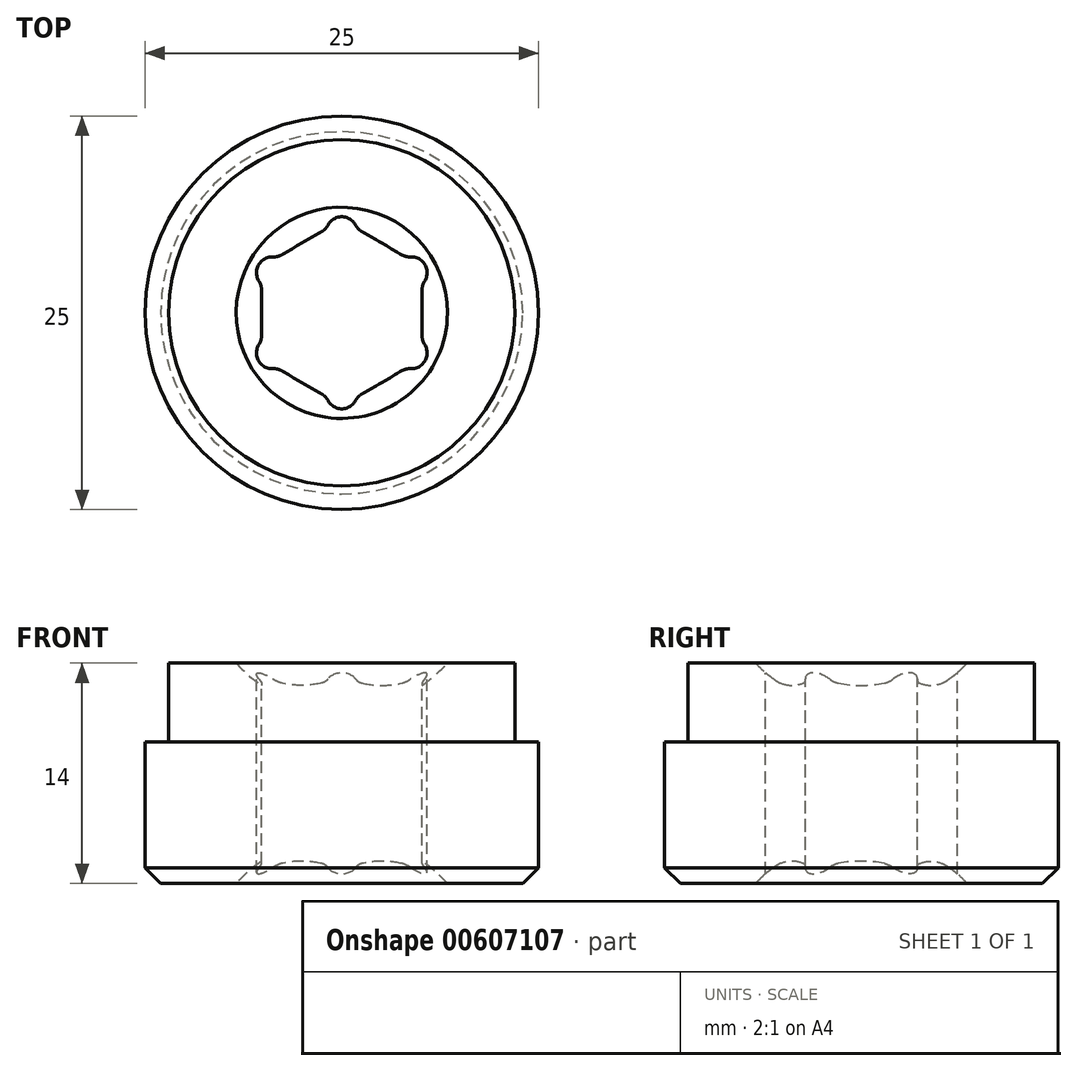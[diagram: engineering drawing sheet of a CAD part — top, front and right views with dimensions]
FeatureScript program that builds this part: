
annotation { "Feature Type Name" : "Feature", "Feature Type Description" : "" }
export const myFeature = defineFeature(function(context is Context, id is Id, definition is map)
    precondition{}
    {
        {
            var Q0;
            Q0=qCreatedBy(makeId("Top.planeOp"),FACE);
            var sketch = newSketch(context, id + "F0", { "sketchPlane" : qUnion([Q0])});
            skCircle(sketch, "E0", {"center": v(0, 0) * mm, "radius": 12.5 * mm});
            skCircle(sketch, "E1.cCircle", {"center": v(0, 0) * mm, "radius": 5.1 * mm, "construction": true});
            skLineSegment(sketch, "E1.0", {"start": v(5.1, -2.94) * mm, "end": v(0, -5.89) * mm});
            skLineSegment(sketch, "E1.1", {"start": v(0, -5.89) * mm, "end": v(-5.1, -2.94) * mm});
            skLineSegment(sketch, "E1.2", {"start": v(-5.1, -2.94) * mm, "end": v(-5.1, 2.94) * mm});
            skLineSegment(sketch, "E1.3", {"start": v(-5.1, 2.94) * mm, "end": v(0, 5.89) * mm});
            skLineSegment(sketch, "E1.4", {"start": v(0, 5.89) * mm, "end": v(5.1, 2.94) * mm});
            skLineSegment(sketch, "E1.5", {"start": v(5.1, 2.94) * mm, "end": v(5.1, -2.94) * mm});
            skPoint(sketch, "E1.0.midPoint", {"position": v(2.55, -4.42) * mm});
            skSolve(sketch);
        }
        {
            var Q0;
            Q0 = qSketchRegion(id + "F0", true);
            extrude(context, id + "F1", {"entities" : qUnion([Q0]), "depth" : 14 * mm, "offsetDistance" : 25 * mm});
        }
        {
            var Q0;
            Q0=makeQuery(id+"F1.opExtrude","CAP_FACE",FACE,{"disambiguationData":[OSD([sQuery(id+"F0.wireOp",EDGE,"E0"),sQuery(id+"F0.wireOp",EDGE,"E1.0"),sQuery(id+"F0.wireOp",EDGE,"E1.1"),sQuery(id+"F0.wireOp",EDGE,"E1.2"),sQuery(id+"F0.wireOp",EDGE,"E1.3"),sQuery(id+"F0.wireOp",EDGE,"E1.4"),sQuery(id+"F0.wireOp",EDGE,"E1.5")])],"isStart":false});
            var sketch = newSketch(context, id + "F2", { "sketchPlane" : qUnion([Q0])});
            skCircle(sketch, "E2", {"center": v(0, 0) * mm, "radius": 11 * mm});
            skCircle(sketch, "E3.0", {"center": v(0, 0) * mm, "radius": 12.5 * mm});
            skSolve(sketch);
        }
        {
            var Q0;
            Q0 = qSketchRegion(id + "F2", true);
            extrude(context, id + "F3", {"entities" : qUnion([Q0]), "operationType" : NewBodyOperationType.REMOVE, "oppositeDirection" : true, "depth" : 5 * mm, "offsetDistance" : 25 * mm});
        }
        {
            var Q0;
            Q0=makeQuery(id+"F1.opExtrude","CAP_FACE",FACE,{"disambiguationData":[OSD([sQuery(id+"F0.wireOp",EDGE,"E0"),sQuery(id+"F0.wireOp",EDGE,"E1.0"),sQuery(id+"F0.wireOp",EDGE,"E1.1"),sQuery(id+"F0.wireOp",EDGE,"E1.2"),sQuery(id+"F0.wireOp",EDGE,"E1.3"),sQuery(id+"F0.wireOp",EDGE,"E1.4"),sQuery(id+"F0.wireOp",EDGE,"E1.5")])],"isStart":false});
            var sketch = newSketch(context, id + "F4", { "sketchPlane" : qUnion([Q0])});
            skCircle(sketch, "E4.cCircle", {"center": v(0, 0) * mm, "radius": 4.42 * mm, "construction": true});
            skLineSegment(sketch, "E4.0", {"start": v(0, 5.1) * mm, "end": v(4.42, 2.55) * mm, "construction": true});
            skLineSegment(sketch, "E4.1", {"start": v(4.42, 2.55) * mm, "end": v(4.42, -2.55) * mm, "construction": true});
            skLineSegment(sketch, "E4.2", {"start": v(4.42, -2.55) * mm, "end": v(0, -5.1) * mm, "construction": true});
            skLineSegment(sketch, "E4.3", {"start": v(0, -5.1) * mm, "end": v(-4.42, -2.55) * mm, "construction": true});
            skLineSegment(sketch, "E4.4", {"start": v(-4.42, -2.55) * mm, "end": v(-4.42, 2.55) * mm, "construction": true});
            skLineSegment(sketch, "E4.5", {"start": v(-4.42, 2.55) * mm, "end": v(0, 5.1) * mm, "construction": true});
            skPoint(sketch, "E4.0.midPoint", {"position": v(2.2, 3.82) * mm});
            skCircle(sketch, "E5", {"center": v(0, 5.1) * mm, "radius": 1 * mm});
            skCircle(sketch, "E6", {"center": v(-4.42, 2.55) * mm, "radius": 1 * mm});
            skCircle(sketch, "E7", {"center": v(-4.42, -2.55) * mm, "radius": 1 * mm});
            skCircle(sketch, "E8", {"center": v(0, -5.1) * mm, "radius": 1 * mm});
            skCircle(sketch, "E9", {"center": v(4.42, -2.55) * mm, "radius": 1 * mm});
            skCircle(sketch, "E10", {"center": v(4.42, 2.55) * mm, "radius": 1 * mm});
            skCircle(sketch, "E11", {"center": v(0, 0) * mm, "radius": 5.1 * mm, "construction": true});
            skSolve(sketch);
        }
        {
            var Q0;
            Q0 = qSketchRegion(id + "F4", true);
            extrude(context, id + "F5", {"entities" : qUnion([Q0]), "operationType" : NewBodyOperationType.REMOVE, "endBound" : BoundingType.THROUGH_ALL, "oppositeDirection" : true, "depth" : 25 * mm, "offsetDistance" : 25 * mm});
        }
        {
            var Q0;
            Q0=makeQuery(id+"F5.boolean.opBoolean","INTERSECT",EDGE,{"derivedFrom":[makeQuery(id+"F1.opExtrude","SWEPT_FACE",FACE,{"disambiguationData":[OSD([sQuery(id+"F0.wireOp",EDGE,"E1.2")])]}),makeQuery(id+"F5.opExtrude","SWEPT_FACE",FACE,{"disambiguationData":[OSD([sQuery(id+"F4.wireOp",EDGE,"E6")])]})]});
            var Q1;
            Q1=makeQuery(id+"F5.boolean.opBoolean","INTERSECT",EDGE,{"derivedFrom":[makeQuery(id+"F1.opExtrude","SWEPT_FACE",FACE,{"disambiguationData":[OSD([sQuery(id+"F0.wireOp",EDGE,"E1.2")])]}),makeQuery(id+"F5.opExtrude","SWEPT_FACE",FACE,{"disambiguationData":[OSD([sQuery(id+"F4.wireOp",EDGE,"E7")])]})]});
            var Q2;
            Q2=makeQuery(id+"F5.boolean.opBoolean","INTERSECT",EDGE,{"derivedFrom":[makeQuery(id+"F1.opExtrude","SWEPT_FACE",FACE,{"disambiguationData":[OSD([sQuery(id+"F0.wireOp",EDGE,"E1.1")])]}),makeQuery(id+"F5.opExtrude","SWEPT_FACE",FACE,{"disambiguationData":[OSD([sQuery(id+"F4.wireOp",EDGE,"E7")])]})]});
            var Q3;
            Q3=makeQuery(id+"F5.boolean.opBoolean","INTERSECT",EDGE,{"derivedFrom":[makeQuery(id+"F1.opExtrude","SWEPT_FACE",FACE,{"disambiguationData":[OSD([sQuery(id+"F0.wireOp",EDGE,"E1.1")])]}),makeQuery(id+"F5.opExtrude","SWEPT_FACE",FACE,{"disambiguationData":[OSD([sQuery(id+"F4.wireOp",EDGE,"E8")])]})]});
            var Q4;
            Q4=makeQuery(id+"F5.boolean.opBoolean","INTERSECT",EDGE,{"derivedFrom":[makeQuery(id+"F1.opExtrude","SWEPT_FACE",FACE,{"disambiguationData":[OSD([sQuery(id+"F0.wireOp",EDGE,"E1.0")])]}),makeQuery(id+"F5.opExtrude","SWEPT_FACE",FACE,{"disambiguationData":[OSD([sQuery(id+"F4.wireOp",EDGE,"E8")])]})]});
            var Q5;
            Q5=makeQuery(id+"F5.boolean.opBoolean","INTERSECT",EDGE,{"derivedFrom":[makeQuery(id+"F1.opExtrude","SWEPT_FACE",FACE,{"disambiguationData":[OSD([sQuery(id+"F0.wireOp",EDGE,"E1.0")])]}),makeQuery(id+"F5.opExtrude","SWEPT_FACE",FACE,{"disambiguationData":[OSD([sQuery(id+"F4.wireOp",EDGE,"E9")])]})]});
            var Q6;
            Q6=makeQuery(id+"F5.boolean.opBoolean","INTERSECT",EDGE,{"derivedFrom":[makeQuery(id+"F1.opExtrude","SWEPT_FACE",FACE,{"disambiguationData":[OSD([sQuery(id+"F0.wireOp",EDGE,"E1.5")])]}),makeQuery(id+"F5.opExtrude","SWEPT_FACE",FACE,{"disambiguationData":[OSD([sQuery(id+"F4.wireOp",EDGE,"E9")])]})]});
            var Q7;
            Q7=makeQuery(id+"F5.boolean.opBoolean","INTERSECT",EDGE,{"derivedFrom":[makeQuery(id+"F1.opExtrude","SWEPT_FACE",FACE,{"disambiguationData":[OSD([sQuery(id+"F0.wireOp",EDGE,"E1.5")])]}),makeQuery(id+"F5.opExtrude","SWEPT_FACE",FACE,{"disambiguationData":[OSD([sQuery(id+"F4.wireOp",EDGE,"E10")])]})]});
            var Q8;
            Q8=makeQuery(id+"F5.boolean.opBoolean","INTERSECT",EDGE,{"derivedFrom":[makeQuery(id+"F1.opExtrude","SWEPT_FACE",FACE,{"disambiguationData":[OSD([sQuery(id+"F0.wireOp",EDGE,"E1.4")])]}),makeQuery(id+"F5.opExtrude","SWEPT_FACE",FACE,{"disambiguationData":[OSD([sQuery(id+"F4.wireOp",EDGE,"E10")])]})]});
            var Q9;
            Q9=makeQuery(id+"F5.boolean.opBoolean","INTERSECT",EDGE,{"derivedFrom":[makeQuery(id+"F1.opExtrude","SWEPT_FACE",FACE,{"disambiguationData":[OSD([sQuery(id+"F0.wireOp",EDGE,"E1.4")])]}),makeQuery(id+"F5.opExtrude","SWEPT_FACE",FACE,{"disambiguationData":[OSD([sQuery(id+"F4.wireOp",EDGE,"E5")])]})]});
            var Q10;
            Q10=makeQuery(id+"F5.boolean.opBoolean","INTERSECT",EDGE,{"derivedFrom":[makeQuery(id+"F1.opExtrude","SWEPT_FACE",FACE,{"disambiguationData":[OSD([sQuery(id+"F0.wireOp",EDGE,"E1.3")])]}),makeQuery(id+"F5.opExtrude","SWEPT_FACE",FACE,{"disambiguationData":[OSD([sQuery(id+"F4.wireOp",EDGE,"E5")])]})]});
            var Q11;
            Q11=makeQuery(id+"F5.boolean.opBoolean","INTERSECT",EDGE,{"derivedFrom":[makeQuery(id+"F1.opExtrude","SWEPT_FACE",FACE,{"disambiguationData":[OSD([sQuery(id+"F0.wireOp",EDGE,"E1.3")])]}),makeQuery(id+"F5.opExtrude","SWEPT_FACE",FACE,{"disambiguationData":[OSD([sQuery(id+"F4.wireOp",EDGE,"E6")])]})]});
            fillet(context, id + "F6", {"entities" : qUnion([Q0, Q1, Q2, Q3, Q4, Q5, Q6, Q7, Q8, Q9, Q10, Q11]), "radius" : 1 * mm, "tangentPropagation" : true, "allowEdgeOverflow" : false});
        }
        {
            var Q0;
            Q0=makeQuery(id+"F3.boolean.opBoolean","COPY",EDGE,{"derivedFrom":makeQuery(id+"F3.opExtrude","CAP_EDGE",EDGE,{"disambiguationData":[OSD([sQuery(id+"F2.wireOp",EDGE,"E2")])],"isStart":true})});
            var Q1;
            Q1=makeQuery(id+"F1.opExtrude","CAP_EDGE",EDGE,{"disambiguationData":[OSD([sQuery(id+"F0.wireOp",EDGE,"E0")])],"isStart":true});
            chamfer(context, id + "F7", {"entities" : qUnion([Q0, Q1]), "width" : 1 * mm, "tangentPropagation" : true});
        }
        {
            var Q0;
            Q0=qCreatedBy(makeId("Right.planeOp"),FACE);
            var sketch = newSketch(context, id + "F8", { "sketchPlane" : qUnion([Q0])});
            skArc(sketch, "E12", {"start": v(0, -15) * mm, "mid": v(9, -6) * mm, "end": v(0, 3) * mm});
            skArc(sketch, "E13", {"start": v(0, 11) * mm, "mid": v(9, 20) * mm, "end": v(0, 29) * mm});
            skLineSegment(sketch, "E14", {"start": v(0, -15) * mm, "end": v(0, 3) * mm});
            skLineSegment(sketch, "E15.trimOffspring", {"start": v(0, 11) * mm, "end": v(0, 29) * mm});
            skSolve(sketch);
        }
        {
            var Q0;
            Q0 = qSketchRegion(id + "F8", true);
            var Q1;
            Q1=sQuery(id+"F8.wireOp",EDGE,"E14");
            revolve(context, id + "F9", {"operationType" : NewBodyOperationType.REMOVE, "entities" : qUnion([Q0]), "axis" : qUnion([Q1]), "revolveType" : RevolveType.FULL, "oppositeDirection" : true});
        }
    });
